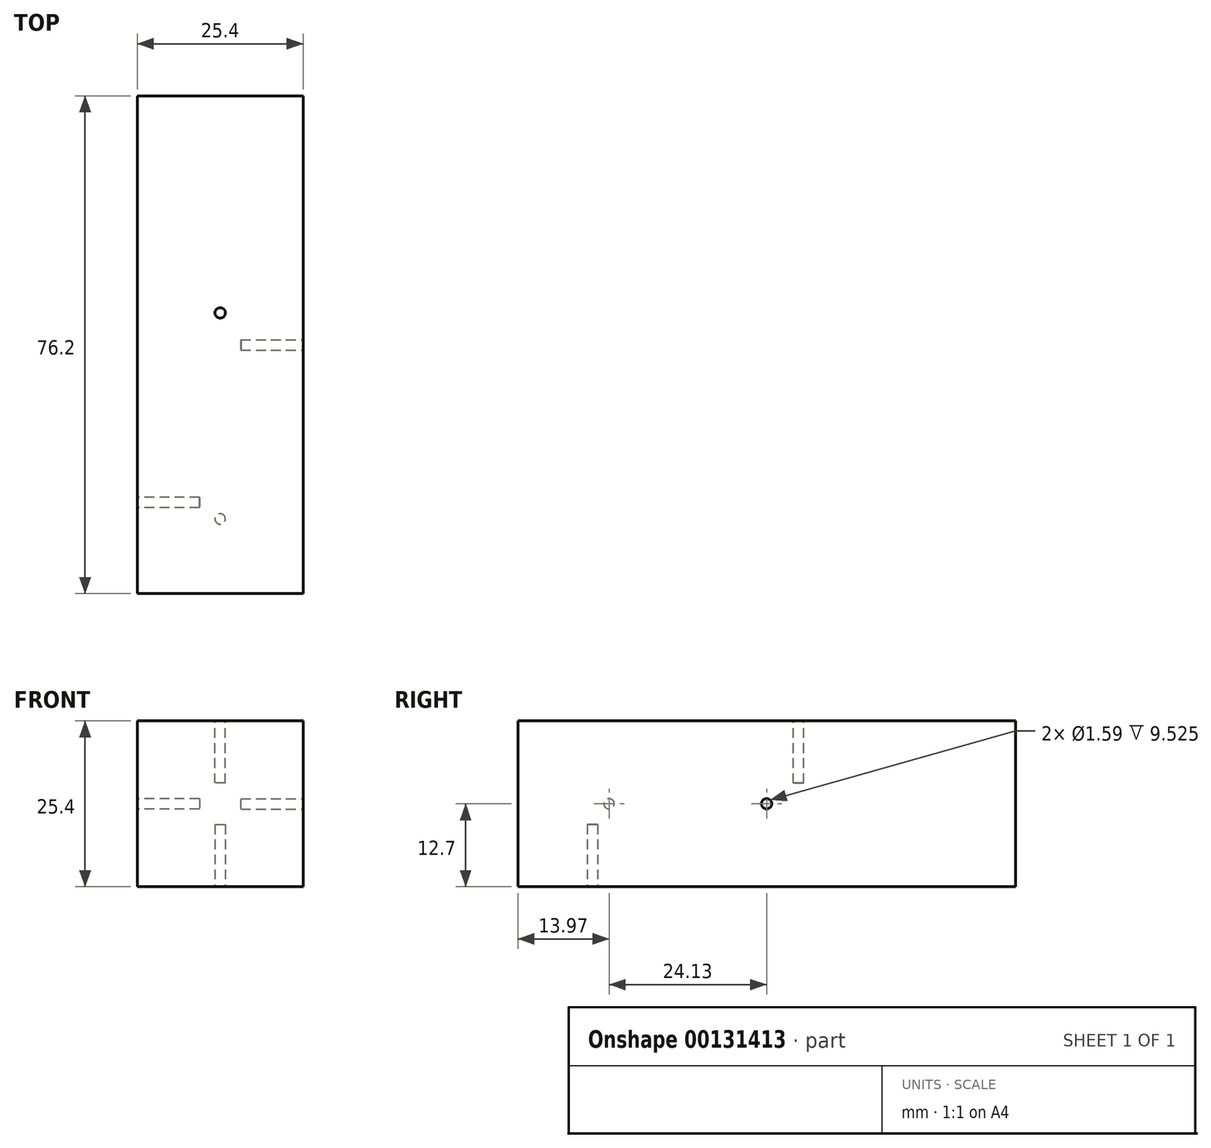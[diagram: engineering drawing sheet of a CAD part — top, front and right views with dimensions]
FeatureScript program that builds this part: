
annotation { "Feature Type Name" : "Feature", "Feature Type Description" : "" }
export const myFeature = defineFeature(function(context is Context, id is Id, definition is map)
    precondition{}
    {
        {
            var Q0;
            Q0=qCreatedBy(makeId("Front.planeOp"),FACE);
            var sketch = newSketch(context, id + "F0", { "sketchPlane" : qUnion([Q0])});
            skLineSegment(sketch, "E0.bottom", {"start": v(-12.7, 12.7) * mm, "end": v(12.7, 12.7) * mm});
            skLineSegment(sketch, "E0.top", {"start": v(-12.7, -12.7) * mm, "end": v(12.7, -12.7) * mm});
            skLineSegment(sketch, "E0.left", {"start": v(-12.7, 12.7) * mm, "end": v(-12.7, -12.7) * mm});
            skLineSegment(sketch, "E0.right", {"start": v(12.7, 12.7) * mm, "end": v(12.7, -12.7) * mm});
            skSolve(sketch);
        }
        {
            var Q0;
            Q0 = qSketchRegion(id + "F0", true);
            extrude(context, id + "F1", {"entities" : qUnion([Q0]), "depth" : 76.2 * mm});
        }
        {
            var Q0;
            Q0=makeQuery(id+"F1.opExtrude","SWEPT_FACE",FACE,{"disambiguationData":[OSD([sQuery(id+"F0.wireOp",EDGE,"E0.bottom")])]});
            var sketch = newSketch(context, id + "F2", { "sketchPlane" : qUnion([Q0])});
            skLineSegment(sketch, "E1", {"start": v(0, 0) * mm, "end": v(0, -76.2) * mm, "construction": true});
            skCircle(sketch, "E2", {"center": v(0, -33.22) * mm, "radius": 0.8 * mm});
            skSolve(sketch);
        }
        {
            var Q0;
            Q0 = qSketchRegion(id + "F2", true);
            extrude(context, id + "F3", {"entities" : qUnion([Q0]), "operationType" : NewBodyOperationType.REMOVE, "oppositeDirection" : true, "depth" : 9.52 * mm});
        }
        {
            var Q0;
            Q0=makeQuery(id+"F1.opExtrude","SWEPT_FACE",FACE,{"disambiguationData":[OSD([sQuery(id+"F0.wireOp",EDGE,"E0.right")])]});
            var sketch = newSketch(context, id + "F4", { "sketchPlane" : qUnion([Q0])});
            skLineSegment(sketch, "E3", {"start": v(0, 0) * mm, "end": v(-76.2, 0) * mm, "construction": true});
            skCircle(sketch, "E4", {"center": v(-38.1, 0) * mm, "radius": 0.8 * mm});
            skSolve(sketch);
        }
        {
            var Q0;
            Q0 = qSketchRegion(id + "F4", true);
            extrude(context, id + "F5", {"entities" : qUnion([Q0]), "operationType" : NewBodyOperationType.REMOVE, "oppositeDirection" : true, "depth" : 9.52 * mm});
        }
        {
            var Q0;
            Q0=makeQuery(id+"F1.opExtrude","SWEPT_FACE",FACE,{"disambiguationData":[OSD([sQuery(id+"F0.wireOp",EDGE,"E0.top")])]});
            var sketch = newSketch(context, id + "F6", { "sketchPlane" : qUnion([Q0])});
            skLineSegment(sketch, "E5", {"start": v(0, 0) * mm, "end": v(0, 76.2) * mm, "construction": true});
            skCircle(sketch, "E6", {"center": v(0, 64.79) * mm, "radius": 0.8 * mm});
            skSolve(sketch);
        }
        {
            var Q0;
            Q0 = qSketchRegion(id + "F6", true);
            extrude(context, id + "F7", {"entities" : qUnion([Q0]), "operationType" : NewBodyOperationType.REMOVE, "oppositeDirection" : true, "depth" : 9.52 * mm});
        }
        {
            var Q0;
            Q0=makeQuery(id+"F1.opExtrude","SWEPT_FACE",FACE,{"disambiguationData":[OSD([sQuery(id+"F0.wireOp",EDGE,"E0.left")])]});
            var sketch = newSketch(context, id + "F8", { "sketchPlane" : qUnion([Q0])});
            skLineSegment(sketch, "E7", {"start": v(0, 0) * mm, "end": v(76.2, 0) * mm, "construction": true});
            skCircle(sketch, "E8", {"center": v(62.23, 0) * mm, "radius": 0.8 * mm});
            skSolve(sketch);
        }
        {
            var Q0;
            Q0 = qSketchRegion(id + "F8", true);
            extrude(context, id + "F9", {"entities" : qUnion([Q0]), "operationType" : NewBodyOperationType.REMOVE, "oppositeDirection" : true, "depth" : 9.52 * mm});
        }
    });
